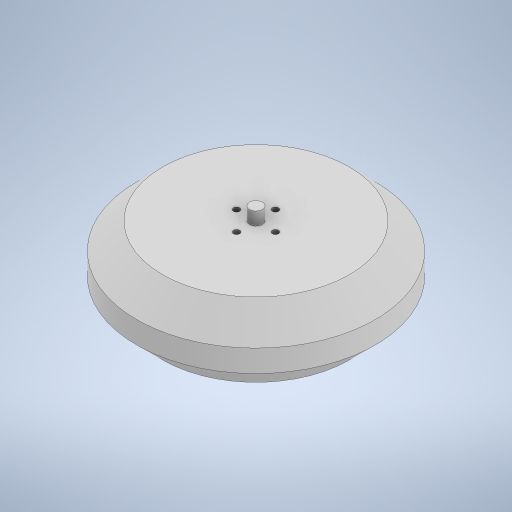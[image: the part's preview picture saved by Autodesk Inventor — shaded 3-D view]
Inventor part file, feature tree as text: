
AUTODESK INVENTOR PART (.ipt)
format: ipt  version: 2023 (Build 270158000, 158)  size: 249,856 bytes
history: native  units: in
note: dims shown in document units (in); Inventor stores cm internally (conversion verified against a paired STEP export)
features: sketch x3, extrude x2, chamfer x1, hole x1
ambient origin geometry x8: Origin, YZ Plane, XZ Plane, XY Plane, X Axis, Y Axis, Z Axis, Center Point
bodies: Solid1 (feature_tree)
feature tree (7):
  extrude  "Extrusion1"  Depth=0.3937in
  chamfer  "Chamfer1"  Distance=0.3937in Angle=45.0deg
  hole  "Hole1"  [1 undecoded]
  extrude  "Extrusion2"  Depth=0.1969in TaperAngle=0.0deg
  sketch  "Sketch1"  dims[d0=1.122in d1=0.0in d2=3.622in d3=0.3937in d4=0.0787in d5=45.0deg]
  sketch  "Sketch2"  dims[d6=0.0968in d7=0.2362in d8=0.1575in d9=0.0787in d10=90.0deg d11=0.3465in d12=0.8108in d13=0.5906in]
  sketch  "Sketch3"  dims[d14=0.1969in d15=0.1969in d16=0.0in]
note: 1 required parameter value undecoded (feature->parameter linkage not recoverable at this tier; creation-order binding heuristic only, values carry confidence <= 0.55)
